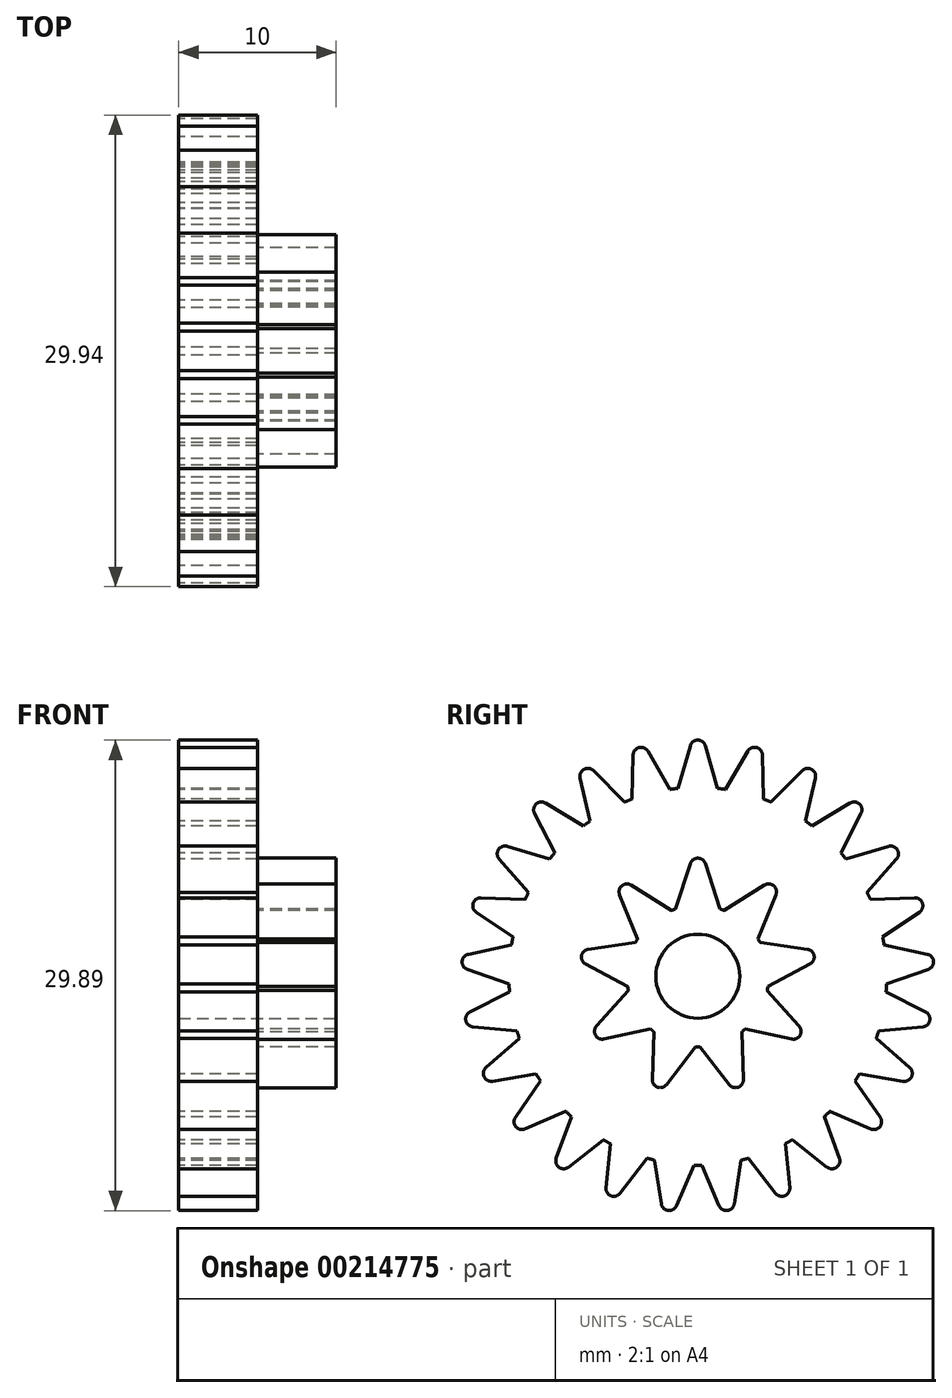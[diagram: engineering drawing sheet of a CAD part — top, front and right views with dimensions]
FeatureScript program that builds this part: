
annotation { "Feature Type Name" : "Feature", "Feature Type Description" : "" }
export const myFeature = defineFeature(function(context is Context, id is Id, definition is map)
    precondition{}
    {
        {
            var Q0;
            Q0=qCreatedBy(makeId("Right.planeOp"),FACE);
            var sketch = newSketch(context, id + "F0", { "sketchPlane" : qUnion([Q0])});
            skArc(sketch, "E0", {"start": v(0.48, 14.64) * mm, "mid": v(0, 15) * mm, "end": v(-0.48, 14.64) * mm});
            skLineSegment(sketch, "E1", {"start": v(-0.48, 14.64) * mm, "end": v(-1.25, 11.93) * mm});
            skLineSegment(sketch, "E2.MirrorCS", {"start": v(0.48, 14.64) * mm, "end": v(1.25, 11.93) * mm});
            skCircle(sketch, "E3", {"center": v(0, 0) * mm, "radius": 12 * mm});
            skLineSegment(sketch, "E4", {"start": v(0, 0) * mm, "end": v(0, 9.86) * mm, "construction": true});
            skLineSegment(sketch, "E5.1.0", {"start": v(-4.1, 14.06) * mm, "end": v(-4.18, 11.25) * mm});
            skArc(sketch, "E5.1.1", {"start": v(-3.17, 14.3) * mm, "mid": v(-3.73, 14.53) * mm, "end": v(-4.1, 14.06) * mm});
            skLineSegment(sketch, "E5.1.2", {"start": v(-3.17, 14.3) * mm, "end": v(-1.76, 11.87) * mm});
            skLineSegment(sketch, "E5.2.0", {"start": v(-7.47, 12.6) * mm, "end": v(-6.85, 9.86) * mm});
            skArc(sketch, "E5.2.1", {"start": v(-6.63, 13.06) * mm, "mid": v(-7.23, 13.14) * mm, "end": v(-7.47, 12.6) * mm});
            skLineSegment(sketch, "E5.2.2", {"start": v(-6.63, 13.06) * mm, "end": v(-4.65, 11.06) * mm});
            skLineSegment(sketch, "E5.3.0", {"start": v(-10.37, 10.34) * mm, "end": v(-9.08, 7.84) * mm});
            skArc(sketch, "E5.3.1", {"start": v(-9.67, 11) * mm, "mid": v(-10.27, 10.93) * mm, "end": v(-10.37, 10.34) * mm});
            skLineSegment(sketch, "E5.3.2", {"start": v(-9.67, 11) * mm, "end": v(-7.26, 9.56) * mm});
            skArc(sketch, "E5.3.3", {"start": v(-9.08, 7.84) * mm, "mid": v(8.21, -8.75) * mm, "end": v(-7.26, 9.56) * mm});
            skLineSegment(sketch, "E5.4.0", {"start": v(-12.62, 7.44) * mm, "end": v(-10.75, 5.34) * mm});
            skArc(sketch, "E5.4.1", {"start": v(-12.1, 8.25) * mm, "mid": v(-12.66, 8.04) * mm, "end": v(-12.62, 7.44) * mm});
            skLineSegment(sketch, "E5.4.2", {"start": v(-12.1, 8.25) * mm, "end": v(-9.4, 7.45) * mm});
            skLineSegment(sketch, "E5.5.0", {"start": v(-14.07, 4.07) * mm, "end": v(-11.74, 2.5) * mm});
            skArc(sketch, "E5.5.1", {"start": v(-13.77, 4.98) * mm, "mid": v(-14.27, 4.64) * mm, "end": v(-14.07, 4.07) * mm});
            skLineSegment(sketch, "E5.5.2", {"start": v(-13.77, 4.98) * mm, "end": v(-10.96, 4.88) * mm});
            skLineSegment(sketch, "E5.6.0", {"start": v(-14.64, 0.44) * mm, "end": v(-11.99, -0.5) * mm});
            skArc(sketch, "E5.6.1", {"start": v(-14.58, 1.4) * mm, "mid": v(-14.97, 0.94) * mm, "end": v(-14.64, 0.44) * mm});
            skLineSegment(sketch, "E5.6.2", {"start": v(-14.58, 1.4) * mm, "end": v(-11.83, 2) * mm});
            skLineSegment(sketch, "E5.7.0", {"start": v(-14.29, -3.22) * mm, "end": v(-11.49, -3.47) * mm});
            skArc(sketch, "E5.7.1", {"start": v(-14.47, -2.27) * mm, "mid": v(-14.73, -2.81) * mm, "end": v(-14.29, -3.22) * mm});
            skLineSegment(sketch, "E5.7.2", {"start": v(-14.47, -2.27) * mm, "end": v(-11.96, -1) * mm});
            skLineSegment(sketch, "E5.8.0", {"start": v(-13.04, -6.67) * mm, "end": v(-10.27, -6.21) * mm});
            skArc(sketch, "E5.8.1", {"start": v(-13.45, -5.8) * mm, "mid": v(-13.57, -6.39) * mm, "end": v(-13.04, -6.67) * mm});
            skLineSegment(sketch, "E5.8.2", {"start": v(-13.45, -5.8) * mm, "end": v(-11.33, -3.95) * mm});
            skLineSegment(sketch, "E5.9.0", {"start": v(-10.97, -9.7) * mm, "end": v(-8.4, -8.57) * mm});
            skArc(sketch, "E5.9.1", {"start": v(-11.58, -8.96) * mm, "mid": v(-11.56, -9.56) * mm, "end": v(-10.97, -9.7) * mm});
            skLineSegment(sketch, "E5.9.2", {"start": v(-11.58, -8.96) * mm, "end": v(-10, -6.64) * mm});
            skLineSegment(sketch, "E5.10.0", {"start": v(-8.21, -12.12) * mm, "end": v(-6, -10.4) * mm});
            skArc(sketch, "E5.10.1", {"start": v(-9, -11.56) * mm, "mid": v(-8.82, -12.14) * mm, "end": v(-8.21, -12.12) * mm});
            skLineSegment(sketch, "E5.10.2", {"start": v(-9, -11.56) * mm, "end": v(-8.03, -8.92) * mm});
            skLineSegment(sketch, "E5.11.0", {"start": v(-4.94, -13.79) * mm, "end": v(-3.23, -11.56) * mm});
            skArc(sketch, "E5.11.1", {"start": v(-5.84, -13.43) * mm, "mid": v(-5.52, -13.95) * mm, "end": v(-4.94, -13.79) * mm});
            skLineSegment(sketch, "E5.11.2", {"start": v(-5.84, -13.43) * mm, "end": v(-5.56, -10.64) * mm});
            skArc(sketch, "E5.11.3", {"start": v(-9.08, 7.84) * mm, "mid": v(8.21, -8.75) * mm, "end": v(-7.26, 9.56) * mm});
            skLineSegment(sketch, "E5.12.0", {"start": v(-1.36, -14.58) * mm, "end": v(-0.25, -12) * mm});
            skArc(sketch, "E5.12.1", {"start": v(-2.31, -14.46) * mm, "mid": v(-1.88, -14.88) * mm, "end": v(-1.36, -14.58) * mm});
            skLineSegment(sketch, "E5.12.2", {"start": v(-2.31, -14.46) * mm, "end": v(-2.74, -11.68) * mm});
            skLineSegment(sketch, "E5.13.0", {"start": v(2.31, -14.46) * mm, "end": v(2.74, -11.68) * mm});
            skArc(sketch, "E5.13.1", {"start": v(1.36, -14.58) * mm, "mid": v(1.88, -14.88) * mm, "end": v(2.31, -14.46) * mm});
            skLineSegment(sketch, "E5.13.2", {"start": v(1.36, -14.58) * mm, "end": v(0.25, -12) * mm});
            skLineSegment(sketch, "E5.14.0", {"start": v(5.84, -13.43) * mm, "end": v(5.56, -10.64) * mm});
            skArc(sketch, "E5.14.1", {"start": v(4.94, -13.79) * mm, "mid": v(5.52, -13.95) * mm, "end": v(5.84, -13.43) * mm});
            skLineSegment(sketch, "E5.14.2", {"start": v(4.94, -13.79) * mm, "end": v(3.23, -11.56) * mm});
            skLineSegment(sketch, "E5.15.0", {"start": v(9, -11.56) * mm, "end": v(8.03, -8.92) * mm});
            skArc(sketch, "E5.15.1", {"start": v(8.21, -12.12) * mm, "mid": v(8.82, -12.14) * mm, "end": v(9, -11.56) * mm});
            skLineSegment(sketch, "E5.15.2", {"start": v(8.21, -12.12) * mm, "end": v(6, -10.4) * mm});
            skArc(sketch, "E5.15.3", {"start": v(-9.08, 7.84) * mm, "mid": v(8.21, -8.75) * mm, "end": v(-7.26, 9.56) * mm});
            skLineSegment(sketch, "E5.16.0", {"start": v(11.58, -8.96) * mm, "end": v(10, -6.64) * mm});
            skArc(sketch, "E5.16.1", {"start": v(10.97, -9.7) * mm, "mid": v(11.56, -9.56) * mm, "end": v(11.58, -8.96) * mm});
            skLineSegment(sketch, "E5.16.2", {"start": v(10.97, -9.7) * mm, "end": v(8.4, -8.57) * mm});
            skLineSegment(sketch, "E5.17.0", {"start": v(13.45, -5.8) * mm, "end": v(11.33, -3.95) * mm});
            skArc(sketch, "E5.17.1", {"start": v(13.04, -6.67) * mm, "mid": v(13.57, -6.39) * mm, "end": v(13.45, -5.8) * mm});
            skLineSegment(sketch, "E5.17.2", {"start": v(13.04, -6.67) * mm, "end": v(10.27, -6.21) * mm});
            skLineSegment(sketch, "E5.18.0", {"start": v(14.47, -2.27) * mm, "end": v(11.96, -1) * mm});
            skArc(sketch, "E5.18.1", {"start": v(14.29, -3.22) * mm, "mid": v(14.73, -2.81) * mm, "end": v(14.47, -2.27) * mm});
            skLineSegment(sketch, "E5.18.2", {"start": v(14.29, -3.22) * mm, "end": v(11.49, -3.47) * mm});
            skLineSegment(sketch, "E5.19.0", {"start": v(14.58, 1.4) * mm, "end": v(11.83, 2) * mm});
            skArc(sketch, "E5.19.1", {"start": v(14.64, 0.44) * mm, "mid": v(14.97, 0.94) * mm, "end": v(14.58, 1.4) * mm});
            skLineSegment(sketch, "E5.19.2", {"start": v(14.64, 0.44) * mm, "end": v(11.99, -0.5) * mm});
            skLineSegment(sketch, "E5.20.0", {"start": v(13.77, 4.98) * mm, "end": v(10.96, 4.88) * mm});
            skArc(sketch, "E5.20.1", {"start": v(14.07, 4.07) * mm, "mid": v(14.27, 4.64) * mm, "end": v(13.77, 4.98) * mm});
            skLineSegment(sketch, "E5.20.2", {"start": v(14.07, 4.07) * mm, "end": v(11.74, 2.5) * mm});
            skLineSegment(sketch, "E5.21.0", {"start": v(12.1, 8.25) * mm, "end": v(9.4, 7.45) * mm});
            skArc(sketch, "E5.21.1", {"start": v(12.62, 7.44) * mm, "mid": v(12.66, 8.04) * mm, "end": v(12.1, 8.25) * mm});
            skLineSegment(sketch, "E5.21.2", {"start": v(12.62, 7.44) * mm, "end": v(10.75, 5.34) * mm});
            skLineSegment(sketch, "E5.22.0", {"start": v(9.67, 11) * mm, "end": v(7.26, 9.56) * mm});
            skArc(sketch, "E5.22.1", {"start": v(10.37, 10.34) * mm, "mid": v(10.27, 10.93) * mm, "end": v(9.67, 11) * mm});
            skLineSegment(sketch, "E5.22.2", {"start": v(10.37, 10.34) * mm, "end": v(9.08, 7.84) * mm});
            skLineSegment(sketch, "E6.2.23.0", {"start": v(6.63, 13.06) * mm, "end": v(4.65, 11.06) * mm});
            skArc(sketch, "E6.3.23.0", {"start": v(7.47, 12.6) * mm, "mid": v(7.23, 13.14) * mm, "end": v(6.63, 13.06) * mm});
            skLineSegment(sketch, "E6.7.23.0", {"start": v(7.47, 12.6) * mm, "end": v(6.85, 9.86) * mm});
            skLineSegment(sketch, "E6.2.24.0", {"start": v(3.17, 14.3) * mm, "end": v(1.76, 11.87) * mm});
            skArc(sketch, "E6.3.24.0", {"start": v(4.1, 14.06) * mm, "mid": v(3.73, 14.53) * mm, "end": v(3.17, 14.3) * mm});
            skLineSegment(sketch, "E6.7.24.0", {"start": v(4.1, 14.06) * mm, "end": v(4.18, 11.25) * mm});
            skSolve(sketch);
        }
        {
            var Q0;
            Q0=qSketchRegion(id+"F0",true);
            extrude(context, id + "F1", {"entities" : qUnion([Q0]), "depth" : 5 * mm});
        }
        {
            var Q0;
            Q0=makeQuery(id+"F1.opExtrude","CAP_FACE",FACE,{"disambiguationData":[OSD([sQuery(id+"F0.wireOp",EDGE,"E0"),sQuery(id+"F0.wireOp",EDGE,"E1"),sQuery(id+"F0.wireOp",EDGE,"E2.MirrorCS"),sQuery(id+"F0.wireOp",EDGE,"E5.1.0"),sQuery(id+"F0.wireOp",EDGE,"E5.1.1"),sQuery(id+"F0.wireOp",EDGE,"E5.1.2"),sQuery(id+"F0.wireOp",EDGE,"E5.2.0"),sQuery(id+"F0.wireOp",EDGE,"E5.2.1"),sQuery(id+"F0.wireOp",EDGE,"E5.2.2"),sQuery(id+"F0.wireOp",EDGE,"E5.3.0"),sQuery(id+"F0.wireOp",EDGE,"E5.3.1"),sQuery(id+"F0.wireOp",EDGE,"E5.3.2"),sQuery(id+"F0.wireOp",EDGE,"E5.4.0"),sQuery(id+"F0.wireOp",EDGE,"E5.4.1"),sQuery(id+"F0.wireOp",EDGE,"E5.4.2"),sQuery(id+"F0.wireOp",EDGE,"E5.5.0"),sQuery(id+"F0.wireOp",EDGE,"E5.5.1"),sQuery(id+"F0.wireOp",EDGE,"E5.5.2"),sQuery(id+"F0.wireOp",EDGE,"E5.6.0"),sQuery(id+"F0.wireOp",EDGE,"E5.6.1"),sQuery(id+"F0.wireOp",EDGE,"E5.6.2"),sQuery(id+"F0.wireOp",EDGE,"E5.7.0"),sQuery(id+"F0.wireOp",EDGE,"E5.7.1"),sQuery(id+"F0.wireOp",EDGE,"E5.7.2"),sQuery(id+"F0.wireOp",EDGE,"E5.8.0"),sQuery(id+"F0.wireOp",EDGE,"E5.8.1"),sQuery(id+"F0.wireOp",EDGE,"E5.8.2"),sQuery(id+"F0.wireOp",EDGE,"E5.9.0"),sQuery(id+"F0.wireOp",EDGE,"E5.9.1"),sQuery(id+"F0.wireOp",EDGE,"E5.9.2"),sQuery(id+"F0.wireOp",EDGE,"E5.10.0"),sQuery(id+"F0.wireOp",EDGE,"E5.10.1"),sQuery(id+"F0.wireOp",EDGE,"E5.10.2"),sQuery(id+"F0.wireOp",EDGE,"E5.11.0"),sQuery(id+"F0.wireOp",EDGE,"E5.11.1"),sQuery(id+"F0.wireOp",EDGE,"E5.11.2"),sQuery(id+"F0.wireOp",EDGE,"E5.12.0"),sQuery(id+"F0.wireOp",EDGE,"E5.12.1"),sQuery(id+"F0.wireOp",EDGE,"E5.12.2"),sQuery(id+"F0.wireOp",EDGE,"E5.13.0"),sQuery(id+"F0.wireOp",EDGE,"E5.13.1"),sQuery(id+"F0.wireOp",EDGE,"E5.13.2"),sQuery(id+"F0.wireOp",EDGE,"E5.14.0"),sQuery(id+"F0.wireOp",EDGE,"E5.14.1"),sQuery(id+"F0.wireOp",EDGE,"E5.14.2"),sQuery(id+"F0.wireOp",EDGE,"E5.15.0"),sQuery(id+"F0.wireOp",EDGE,"E5.15.1"),sQuery(id+"F0.wireOp",EDGE,"E5.15.2"),sQuery(id+"F0.wireOp",EDGE,"E5.16.0"),sQuery(id+"F0.wireOp",EDGE,"E5.16.1"),sQuery(id+"F0.wireOp",EDGE,"E5.16.2"),sQuery(id+"F0.wireOp",EDGE,"E5.17.0"),sQuery(id+"F0.wireOp",EDGE,"E5.17.1"),sQuery(id+"F0.wireOp",EDGE,"E5.17.2"),sQuery(id+"F0.wireOp",EDGE,"E5.18.0"),sQuery(id+"F0.wireOp",EDGE,"E5.18.1"),sQuery(id+"F0.wireOp",EDGE,"E5.18.2"),sQuery(id+"F0.wireOp",EDGE,"E5.19.0"),sQuery(id+"F0.wireOp",EDGE,"E5.19.1"),sQuery(id+"F0.wireOp",EDGE,"E5.19.2"),sQuery(id+"F0.wireOp",EDGE,"E5.20.0"),sQuery(id+"F0.wireOp",EDGE,"E5.20.1"),sQuery(id+"F0.wireOp",EDGE,"E5.20.2"),sQuery(id+"F0.wireOp",EDGE,"E5.21.0"),sQuery(id+"F0.wireOp",EDGE,"E5.21.1"),sQuery(id+"F0.wireOp",EDGE,"E5.21.2"),sQuery(id+"F0.wireOp",EDGE,"E5.22.0"),sQuery(id+"F0.wireOp",EDGE,"E5.22.1"),sQuery(id+"F0.wireOp",EDGE,"E5.22.2"),sQuery(id+"F0.wireOp",EDGE,"E6.2.23.0"),sQuery(id+"F0.wireOp",EDGE,"E6.3.23.0"),sQuery(id+"F0.wireOp",EDGE,"E6.7.23.0"),sQuery(id+"F0.wireOp",EDGE,"E6.2.24.0"),sQuery(id+"F0.wireOp",EDGE,"E6.3.24.0"),sQuery(id+"F0.wireOp",EDGE,"E6.7.24.0"),sQuery(id+"F0.wireOp",EDGE,"E3")])],"isStart":false});
            var sketch = newSketch(context, id + "F2", { "sketchPlane" : qUnion([Q0])});
            skCircle(sketch, "E7", {"center": v(0, 0) * mm, "radius": 7.5 * mm, "construction": true});
            skArc(sketch, "E8", {"start": v(0.48, 7.15) * mm, "mid": v(0, 7.5) * mm, "end": v(-0.48, 7.15) * mm});
            skLineSegment(sketch, "E9", {"start": v(-0.48, 7.15) * mm, "end": v(-1.41, 4.27) * mm});
            skLineSegment(sketch, "E10", {"start": v(0, 3.4) * mm, "end": v(0, 1.15) * mm, "construction": true});
            skLineSegment(sketch, "E11.MirrorCS", {"start": v(0.48, 7.15) * mm, "end": v(1.41, 4.27) * mm});
            skLineSegment(sketch, "E12.1.0", {"start": v(-4.96, 5.18) * mm, "end": v(-3.83, 2.37) * mm});
            skArc(sketch, "E12.1.1", {"start": v(-4.23, 5.79) * mm, "mid": v(-4.82, 5.75) * mm, "end": v(-4.96, 5.18) * mm});
            skLineSegment(sketch, "E12.1.2", {"start": v(-4.23, 5.79) * mm, "end": v(-1.66, 4.18) * mm});
            skLineSegment(sketch, "E12.2.0", {"start": v(-7.13, 0.77) * mm, "end": v(-4.45, -0.65) * mm});
            skArc(sketch, "E12.2.1", {"start": v(-6.96, 1.71) * mm, "mid": v(-7.39, 1.3) * mm, "end": v(-7.13, 0.77) * mm});
            skLineSegment(sketch, "E12.2.2", {"start": v(-6.96, 1.71) * mm, "end": v(-3.96, 2.13) * mm});
            skLineSegment(sketch, "E12.3.0", {"start": v(-5.96, -3.99) * mm, "end": v(-3, -3.36) * mm});
            skArc(sketch, "E12.3.1", {"start": v(-6.43, -3.17) * mm, "mid": v(-6.5, -3.75) * mm, "end": v(-5.96, -3.99) * mm});
            skLineSegment(sketch, "E12.3.2", {"start": v(-6.43, -3.17) * mm, "end": v(-4.4, -0.91) * mm});
            skLineSegment(sketch, "E12.4.0", {"start": v(-2, -6.89) * mm, "end": v(-0.13, -4.5) * mm});
            skArc(sketch, "E12.4.1", {"start": v(-2.9, -6.56) * mm, "mid": v(-2.57, -7.05) * mm, "end": v(-2, -6.89) * mm});
            skLineSegment(sketch, "E12.4.2", {"start": v(-2.9, -6.56) * mm, "end": v(-2.79, -3.53) * mm});
            skLineSegment(sketch, "E12.5.0", {"start": v(2.9, -6.56) * mm, "end": v(2.79, -3.53) * mm});
            skArc(sketch, "E12.5.1", {"start": v(2, -6.89) * mm, "mid": v(2.57, -7.05) * mm, "end": v(2.9, -6.56) * mm});
            skLineSegment(sketch, "E12.5.2", {"start": v(2, -6.89) * mm, "end": v(0.13, -4.5) * mm});
            skLineSegment(sketch, "E12.6.0", {"start": v(6.43, -3.17) * mm, "end": v(4.4, -0.91) * mm});
            skArc(sketch, "E12.6.1", {"start": v(5.96, -3.99) * mm, "mid": v(6.5, -3.75) * mm, "end": v(6.43, -3.17) * mm});
            skLineSegment(sketch, "E12.6.2", {"start": v(5.96, -3.99) * mm, "end": v(3, -3.36) * mm});
            skLineSegment(sketch, "E12.7.0", {"start": v(6.96, 1.71) * mm, "end": v(3.96, 2.13) * mm});
            skArc(sketch, "E12.7.1", {"start": v(7.13, 0.77) * mm, "mid": v(7.39, 1.3) * mm, "end": v(6.96, 1.71) * mm});
            skLineSegment(sketch, "E12.7.2", {"start": v(7.13, 0.77) * mm, "end": v(4.45, -0.65) * mm});
            skLineSegment(sketch, "E12.8.0", {"start": v(4.23, 5.79) * mm, "end": v(1.66, 4.18) * mm});
            skArc(sketch, "E12.8.1", {"start": v(4.96, 5.18) * mm, "mid": v(4.82, 5.75) * mm, "end": v(4.23, 5.79) * mm});
            skLineSegment(sketch, "E12.8.2", {"start": v(4.96, 5.18) * mm, "end": v(3.83, 2.37) * mm});
            skArc(sketch, "E13.trimOffspring", {"start": v(-1.41, 4.27) * mm, "mid": v(-1.54, 4.23) * mm, "end": v(-1.66, 4.18) * mm});
            skArc(sketch, "E14.trimOffspring", {"start": v(1.66, 4.18) * mm, "mid": v(1.54, 4.23) * mm, "end": v(1.41, 4.27) * mm});
            skArc(sketch, "E15.trimOffspring", {"start": v(3.96, 2.13) * mm, "mid": v(3.9, 2.25) * mm, "end": v(3.83, 2.37) * mm});
            skArc(sketch, "E16.trimOffspring", {"start": v(-4.45, -0.65) * mm, "mid": v(-4.43, -0.78) * mm, "end": v(-4.4, -0.91) * mm});
            skArc(sketch, "E17.trimOffspring", {"start": v(-3, -3.36) * mm, "mid": v(-2.9, -3.45) * mm, "end": v(-2.79, -3.53) * mm});
            skArc(sketch, "E18.trimOffspring", {"start": v(-0.13, -4.5) * mm, "mid": v(0, -4.5) * mm, "end": v(0.13, -4.5) * mm});
            skArc(sketch, "E19.trimOffspring", {"start": v(2.79, -3.53) * mm, "mid": v(2.9, -3.45) * mm, "end": v(3, -3.36) * mm});
            skArc(sketch, "E20.trimOffspring", {"start": v(4.4, -0.91) * mm, "mid": v(4.43, -0.78) * mm, "end": v(4.45, -0.65) * mm});
            skArc(sketch, "E21", {"start": v(-3.83, 2.37) * mm, "mid": v(-3.9, 2.25) * mm, "end": v(-3.96, 2.13) * mm});
            skSolve(sketch);
        }
        {
            var Q0;
            Q0=makeQuery(id+"F2.imprint","IMPRINT",FACE,{"disambiguationData":[TD([[makeQuery(id+"F2.imprint","IMPRINT",EDGE,{"derivedFrom":sQuery(id+"F2.wireOp",EDGE,"E8")}),1.0]])]});
            extrude(context, id + "F3", {"entities" : qUnion([Q0]), "operationType" : NewBodyOperationType.ADD, "depth" : 5 * mm});
        }
        {
            var Q0;
            Q0=makeQuery(id+"F3.opExtrude","CAP_FACE",FACE,{"disambiguationData":[OSD([sQuery(id+"F2.wireOp",EDGE,"E8"),sQuery(id+"F2.wireOp",EDGE,"E9"),sQuery(id+"F2.wireOp",EDGE,"E11.MirrorCS"),sQuery(id+"F2.wireOp",EDGE,"E12.1.0"),sQuery(id+"F2.wireOp",EDGE,"E12.1.1"),sQuery(id+"F2.wireOp",EDGE,"E12.1.2"),sQuery(id+"F2.wireOp",EDGE,"E12.2.0"),sQuery(id+"F2.wireOp",EDGE,"E12.2.1"),sQuery(id+"F2.wireOp",EDGE,"E12.2.2"),sQuery(id+"F2.wireOp",EDGE,"E12.3.0"),sQuery(id+"F2.wireOp",EDGE,"E12.3.1"),sQuery(id+"F2.wireOp",EDGE,"E12.3.2"),sQuery(id+"F2.wireOp",EDGE,"E12.4.0"),sQuery(id+"F2.wireOp",EDGE,"E12.4.1"),sQuery(id+"F2.wireOp",EDGE,"E12.4.2"),sQuery(id+"F2.wireOp",EDGE,"E12.5.0"),sQuery(id+"F2.wireOp",EDGE,"E12.5.1"),sQuery(id+"F2.wireOp",EDGE,"E12.5.2"),sQuery(id+"F2.wireOp",EDGE,"E12.6.0"),sQuery(id+"F2.wireOp",EDGE,"E12.6.1"),sQuery(id+"F2.wireOp",EDGE,"E12.6.2"),sQuery(id+"F2.wireOp",EDGE,"E12.7.0"),sQuery(id+"F2.wireOp",EDGE,"E12.7.1"),sQuery(id+"F2.wireOp",EDGE,"E12.7.2"),sQuery(id+"F2.wireOp",EDGE,"E12.8.0"),sQuery(id+"F2.wireOp",EDGE,"E12.8.1"),sQuery(id+"F2.wireOp",EDGE,"E12.8.2"),sQuery(id+"F2.wireOp",EDGE,"E13.trimOffspring"),sQuery(id+"F2.wireOp",EDGE,"E14.trimOffspring"),sQuery(id+"F2.wireOp",EDGE,"E15.trimOffspring"),sQuery(id+"F2.wireOp",EDGE,"E16.trimOffspring"),sQuery(id+"F2.wireOp",EDGE,"E17.trimOffspring"),sQuery(id+"F2.wireOp",EDGE,"E18.trimOffspring"),sQuery(id+"F2.wireOp",EDGE,"E19.trimOffspring"),sQuery(id+"F2.wireOp",EDGE,"E20.trimOffspring"),sQuery(id+"F2.wireOp",EDGE,"E21")])],"isStart":false});
            var sketch = newSketch(context, id + "F4", { "sketchPlane" : qUnion([Q0])});
            skCircle(sketch, "E22", {"center": v(0, 0) * mm, "radius": 2.66 * mm});
            skSolve(sketch);
        }
        {
            var Q0;
            Q0=makeQuery(id+"F4.imprint","IMPRINT",FACE,{"disambiguationData":[TD([[makeQuery(id+"F4.imprint","IMPRINT",EDGE,{"derivedFrom":sQuery(id+"F4.wireOp",EDGE,"E22")}),1.0]])]});
            extrude(context, id + "F5", {"entities" : qUnion([Q0]), "operationType" : NewBodyOperationType.REMOVE, "endBound" : BoundingType.THROUGH_ALL, "oppositeDirection" : true, "depth" : 25 * mm});
        }
    });
